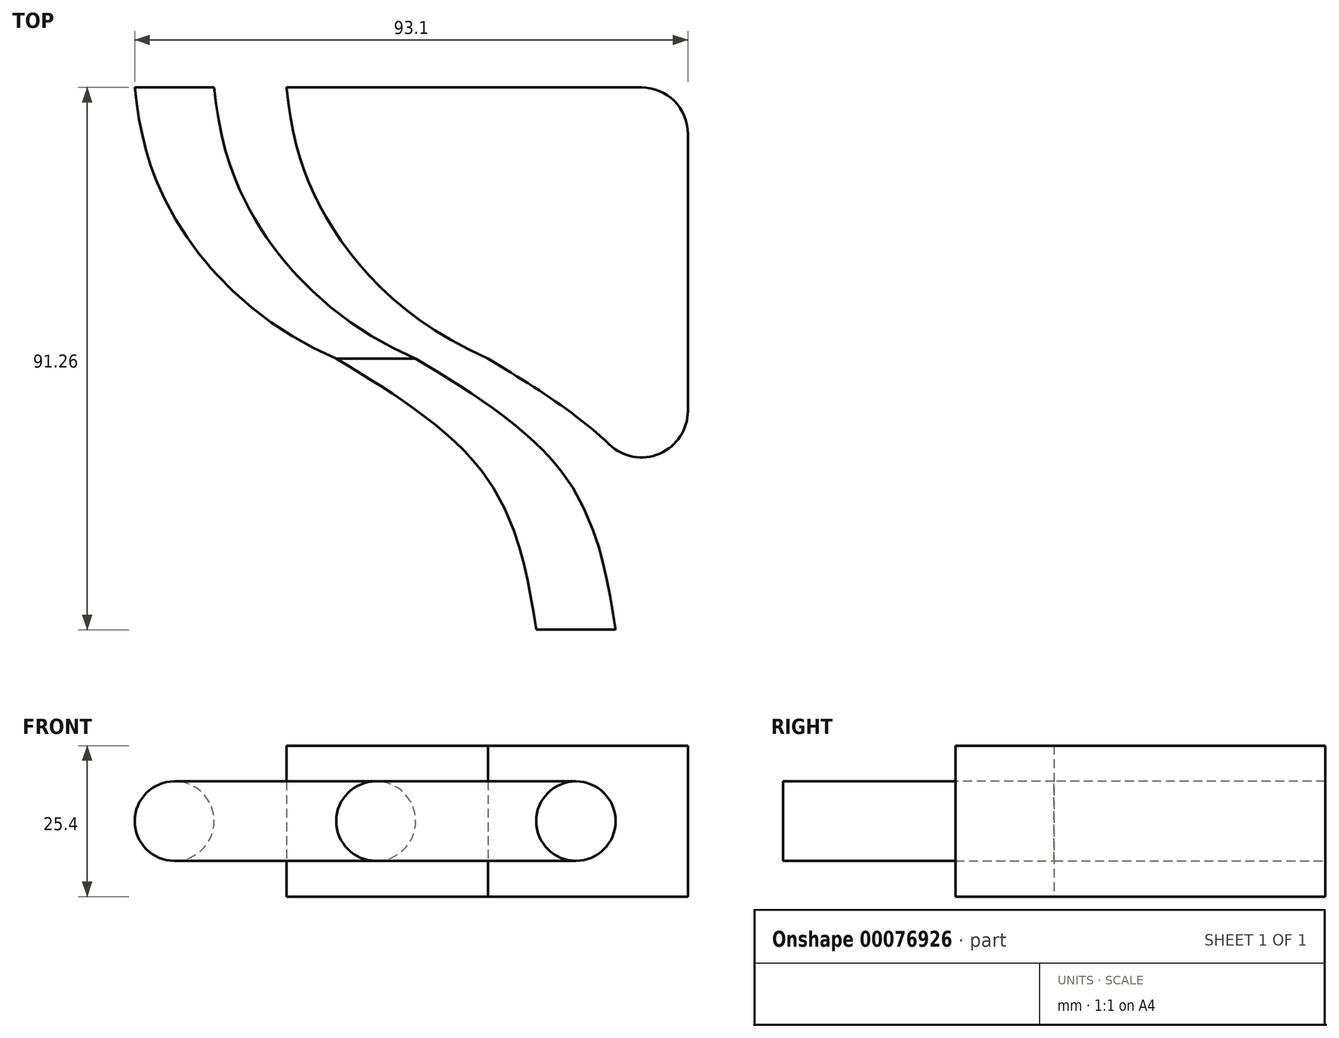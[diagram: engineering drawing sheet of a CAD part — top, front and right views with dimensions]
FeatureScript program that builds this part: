
annotation { "Feature Type Name" : "Feature", "Feature Type Description" : "" }
export const myFeature = defineFeature(function(context is Context, id is Id, definition is map)
    precondition{}
    {
        {
            var Q0;
            Q0=qCreatedBy(makeId("Top.planeOp"),FACE);
            var sketch = newSketch(context, id + "F0", { "sketchPlane" : qUnion([Q0])});
            skLineSegment(sketch, "E0.bottom", {"start": v(52.5, 45.63) * mm, "end": v(-52.5, 45.63) * mm});
            skLineSegment(sketch, "E0.top", {"start": v(52.5, -45.63) * mm, "end": v(-52.5, -45.63) * mm});
            skLineSegment(sketch, "E0.left", {"start": v(52.5, 45.63) * mm, "end": v(52.5, -45.63) * mm});
            skLineSegment(sketch, "E0.right", {"start": v(-52.5, 45.63) * mm, "end": v(-52.5, -45.63) * mm});
            skPoint(sketch, "E0.middle", {"position": v(0, 0) * mm});
            skLineSegment(sketch, "E1", {"start": v(0, 45.63) * mm, "end": v(0, -45.63) * mm, "construction": true});
            skFitSpline(sketch, "E2", {"points": [v(-33.92, 45.63) * mm, v(-26.84, 23.16) * mm, v(0, 0) * mm], "startDerivative": vector(6.88, -63.22) * mm, "endDerivative": vector(75.7, -33.25) * mm});
            skFitSpline(sketch, "E3", {"points": [v(0, 0) * mm, v(25.36, -20.1) * mm, v(33.66, -45.63) * mm], "startDerivative": vector(57.5, -34.48) * mm, "endDerivative": vector(9.33, -60.8) * mm});
            skLineSegment(sketch, "E4", {"start": v(33.66, -45.63) * mm, "end": v(52.5, -45.63) * mm, "construction": true});
            skSolve(sketch);
        }
        {
            var Q0;
            {var subQ1=sQuery(id+"F0.wireOp",EDGE,"E0.right");Q0=makeQuery(id+"F0.imprint","IMPRINT",FACE,{"disambiguationData":[TD([[makeQuery(id+"F0.imprint","IMPRINT",EDGE,{"derivedFrom":subQ1}),1.0]])]});}
            var Q1;
            {var subQ1=sQuery(id+"F0.wireOp",EDGE,"E0.left");Q1=makeQuery(id+"F0.imprint","IMPRINT",FACE,{"disambiguationData":[TD([[makeQuery(id+"F0.imprint","IMPRINT",EDGE,{"derivedFrom":subQ1}),-1.0]])]});}
            extrude(context, id + "F1", {"entities" : qUnion([Q0, Q1]), "endBound" : BoundingType.SYMMETRIC, "depth" : 25.4 * mm});
        }
        {
            var Q0;
            Q0=makeQuery(id+"F1.opExtrude","SWEPT_FACE",FACE,{"disambiguationData":[OSD([sQuery(id+"F0.wireOp",EDGE,"E0.top")])]});
            var sketch = newSketch(context, id + "F2", { "sketchPlane" : qUnion([Q0])});
            skLineSegment(sketch, "E5.0", {"start": v(52.5, 0) * mm, "end": v(-52.5, 0) * mm});
            skFitSpline(sketch, "E6.0", {"points": [v(0, 0) * mm, v(9.87, 0) * mm, v(29.04, 0) * mm, v(32.15, 0) * mm, v(33.66, 0) * mm]});
            skCircle(sketch, "E7", {"center": v(33.66, 0) * mm, "radius": 6.68 * mm});
            skSolve(sketch);
        }
        {
            var Q0;
            {var subQ0=sQuery(id+"F2.wireOp",EDGE,"E6.0");var subQ1=sQuery(id+"F2.wireOp",EDGE,"E5.0");var subQ2=makeQuery(id+"F2.imprint","INTERSECT",VERTEX,{"disambiguationData":[OD(1.0)],"derivedFrom":[subQ1,subQ0]});Q0=makeQuery(id+"F2.imprint","IMPRINT",FACE,{"disambiguationData":[TD([[makeQuery(id+"F2.imprint","IMPRINT",EDGE,{"disambiguationData":[TD([[subQ2,1.0]])],"derivedFrom":subQ1}),1.0]])]});}
            var Q1;
            {var subQ0=sQuery(id+"F2.wireOp",EDGE,"E6.0");var subQ1=sQuery(id+"F2.wireOp",EDGE,"E5.0");var subQ2=makeQuery(id+"F2.imprint","INTERSECT",VERTEX,{"disambiguationData":[OD(1.0)],"derivedFrom":[subQ1,subQ0]});Q1=makeQuery(id+"F2.imprint","IMPRINT",FACE,{"disambiguationData":[TD([[makeQuery(id+"F2.imprint","IMPRINT",EDGE,{"disambiguationData":[TD([[subQ2,1.0]])],"derivedFrom":subQ1}),-1.0]])]});}
            var Q2;
            Q2=sQuery(id+"F0.wireOp",EDGE,"E3");
            var Q3;
            Q3=sQuery(id+"F0.wireOp",EDGE,"E2");
            sweep(context, id + "F3", {"operationType" : NewBodyOperationType.REMOVE, "profiles" : qUnion([Q0, Q1]), "path" : qUnion([Q2, Q3]), "keepProfileOrientation" : true});
        }
        {
            var Q0;
            Q0=makeQuery(id+"F1.opExtrude","SWEPT_EDGE",EDGE,{"disambiguationData":[OSD([sQuery(id+"F0.wireOp",EDGE,"E0.top"),sQuery(id+"F0.wireOp",EDGE,"E0.right")])]});
            var Q1;
            Q1=makeQuery(id+"F1.opExtrude","SWEPT_EDGE",EDGE,{"disambiguationData":[OSD([sQuery(id+"F0.wireOp",EDGE,"E0.top"),sQuery(id+"F0.wireOp",EDGE,"E0.left")])]});
            var Q2;
            Q2=makeQuery(id+"F1.opExtrude","SWEPT_EDGE",EDGE,{"disambiguationData":[OSD([sQuery(id+"F0.wireOp",EDGE,"E0.bottom"),sQuery(id+"F0.wireOp",EDGE,"E0.right")])]});
            var Q3;
            Q3=makeQuery(id+"F1.opExtrude","SWEPT_EDGE",EDGE,{"disambiguationData":[OSD([sQuery(id+"F0.wireOp",EDGE,"E0.bottom"),sQuery(id+"F0.wireOp",EDGE,"E0.left")])]});
            fillet(context, id + "F4", {"entities" : qUnion([Q0, Q1, Q2, Q3]), "radius" : 7.82 * mm, "tangentPropagation" : true, "allowEdgeOverflow" : false});
        }
        {
            var Q0;
            Q0=makeQuery(id+"F1.opExtrude","SWEPT_FACE",FACE,{"disambiguationData":[OSD([sQuery(id+"F0.wireOp",EDGE,"E0.top")])]});
            var sketch = newSketch(context, id + "F5", { "sketchPlane" : qUnion([Q0])});
            skCircle(sketch, "E8", {"center": v(0, 0) * mm, "radius": 6.68 * mm});
            skSolve(sketch);
        }
        {
            var Q0;
            Q0=makeQuery(id+"F5.imprint","IMPRINT",FACE,{"disambiguationData":[TD([[makeQuery(id+"F5.imprint","IMPRINT",EDGE,{"derivedFrom":sQuery(id+"F5.wireOp",EDGE,"E8")}),1.0]])]});
            extrude(context, id + "F6", {"entities" : qUnion([Q0]), "operationType" : NewBodyOperationType.REMOVE, "endBound" : BoundingType.UP_TO_NEXT, "oppositeDirection" : true, "depth" : 45.32 * mm});
        }
    });
